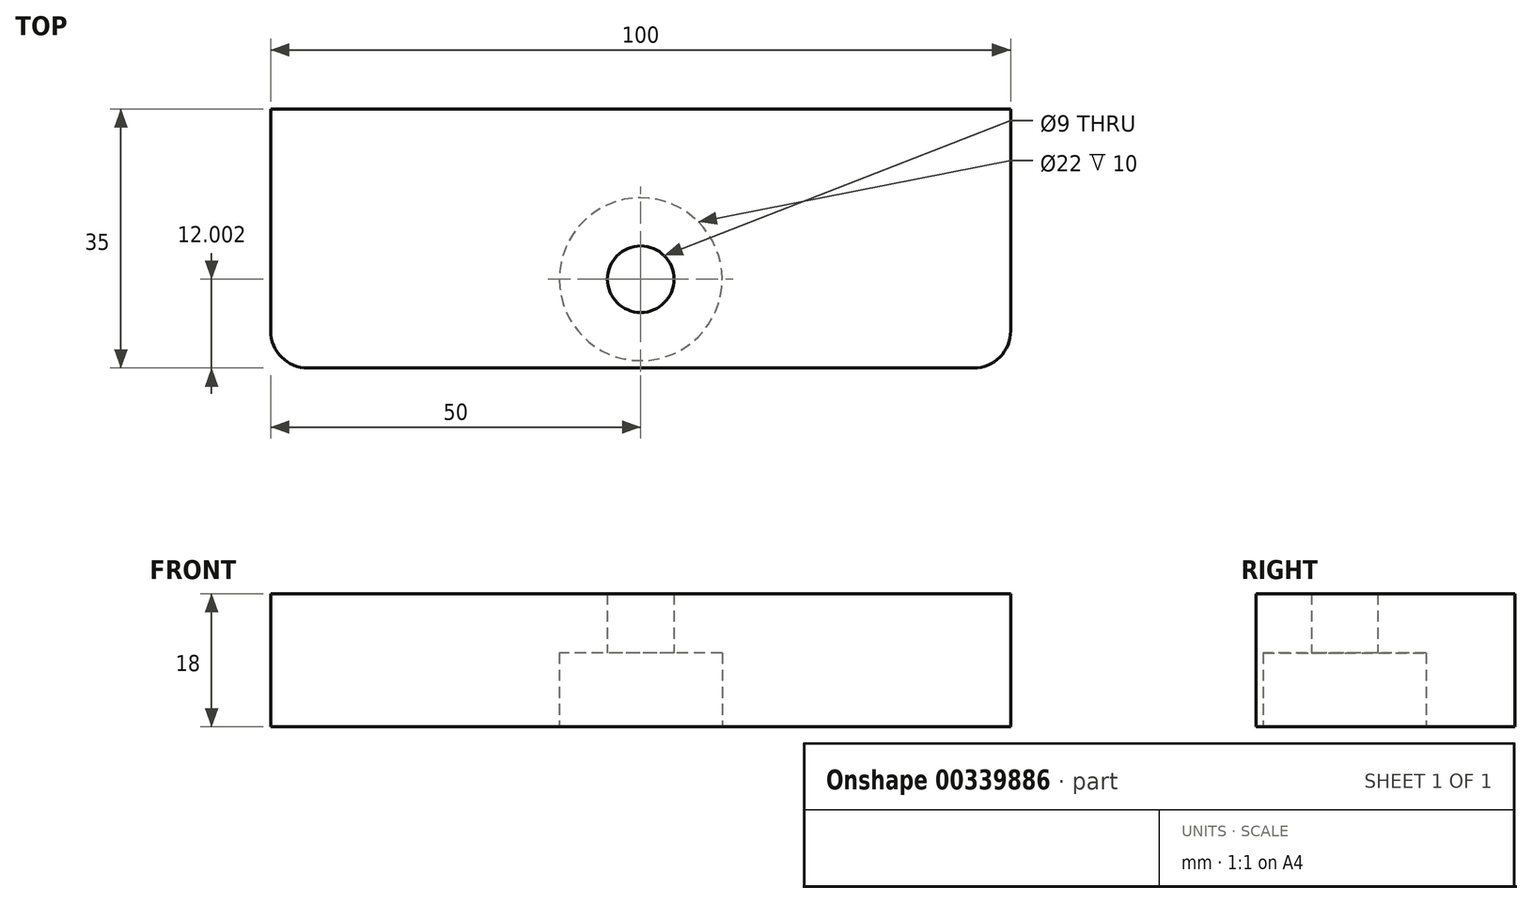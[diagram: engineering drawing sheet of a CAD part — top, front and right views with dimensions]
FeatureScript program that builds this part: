
annotation { "Feature Type Name" : "Feature", "Feature Type Description" : "" }
export const myFeature = defineFeature(function(context is Context, id is Id, definition is map)
    precondition{}
    {
        {
            var Q0;
            Q0=qCreatedBy(makeId("Top.planeOp"),FACE);
            var sketch = newSketch(context, id + "F0", { "sketchPlane" : qUnion([Q0])});
            skCircle(sketch, "E0", {"center": v(-16.25, 9.28) * mm, "radius": 4.5 * mm});
            skCircle(sketch, "E1", {"center": v(-16.25, 9.28) * mm, "radius": 11 * mm});
            skLineSegment(sketch, "E2", {"start": v(-66.25, 32.28) * mm, "end": v(-66.25, -2.72) * mm});
            skLineSegment(sketch, "E3", {"start": v(33.75, 32.28) * mm, "end": v(33.75, -2.72) * mm});
            skLineSegment(sketch, "E4", {"start": v(-66.25, 32.28) * mm, "end": v(33.75, 32.28) * mm});
            skLineSegment(sketch, "E5", {"start": v(33.75, -2.72) * mm, "end": v(-66.25, -2.72) * mm});
            skSolve(sketch);
        }
        {
            var Q0;
            Q0=makeQuery(id+"F0.imprint","IMPRINT",FACE,{"disambiguationData":[TD([[makeQuery(id+"F0.imprint","IMPRINT",EDGE,{"derivedFrom":sQuery(id+"F0.wireOp",EDGE,"E1")}),-1.0]])]});
            var Q1;
            Q1=makeQuery(id+"F0.imprint","IMPRINT",FACE,{"disambiguationData":[TD([[makeQuery(id+"F0.imprint","IMPRINT",EDGE,{"derivedFrom":sQuery(id+"F0.wireOp",EDGE,"E0")}),-1.0]])]});
            extrude(context, id + "F1", {"entities" : qUnion([Q0, Q1]), "depth" : 18 * mm, "offsetDistance" : 25 * mm});
        }
        {
            var Q0;
            Q0=makeQuery(id+"F0.imprint","IMPRINT",FACE,{"disambiguationData":[TD([[makeQuery(id+"F0.imprint","IMPRINT",EDGE,{"derivedFrom":sQuery(id+"F0.wireOp",EDGE,"E0")}),-1.0]])]});
            extrude(context, id + "F2", {"entities" : qUnion([Q0]), "operationType" : NewBodyOperationType.REMOVE, "depth" : 10 * mm, "offsetDistance" : 25 * mm});
        }
        {
            var Q0;
            Q0=makeQuery(id+"F1.opExtrude","SWEPT_EDGE",EDGE,{"disambiguationData":[OSD([sQuery(id+"F0.wireOp",EDGE,"E3"),sQuery(id+"F0.wireOp",EDGE,"E5")])]});
            var Q1;
            Q1=makeQuery(id+"F1.opExtrude","SWEPT_EDGE",EDGE,{"disambiguationData":[OSD([sQuery(id+"F0.wireOp",EDGE,"E2"),sQuery(id+"F0.wireOp",EDGE,"E5")])]});
            fillet(context, id + "F3", {"entities" : qUnion([Q0, Q1]), "radius" : 5 * mm, "tangentPropagation" : true, "allowEdgeOverflow" : false});
        }
    });
